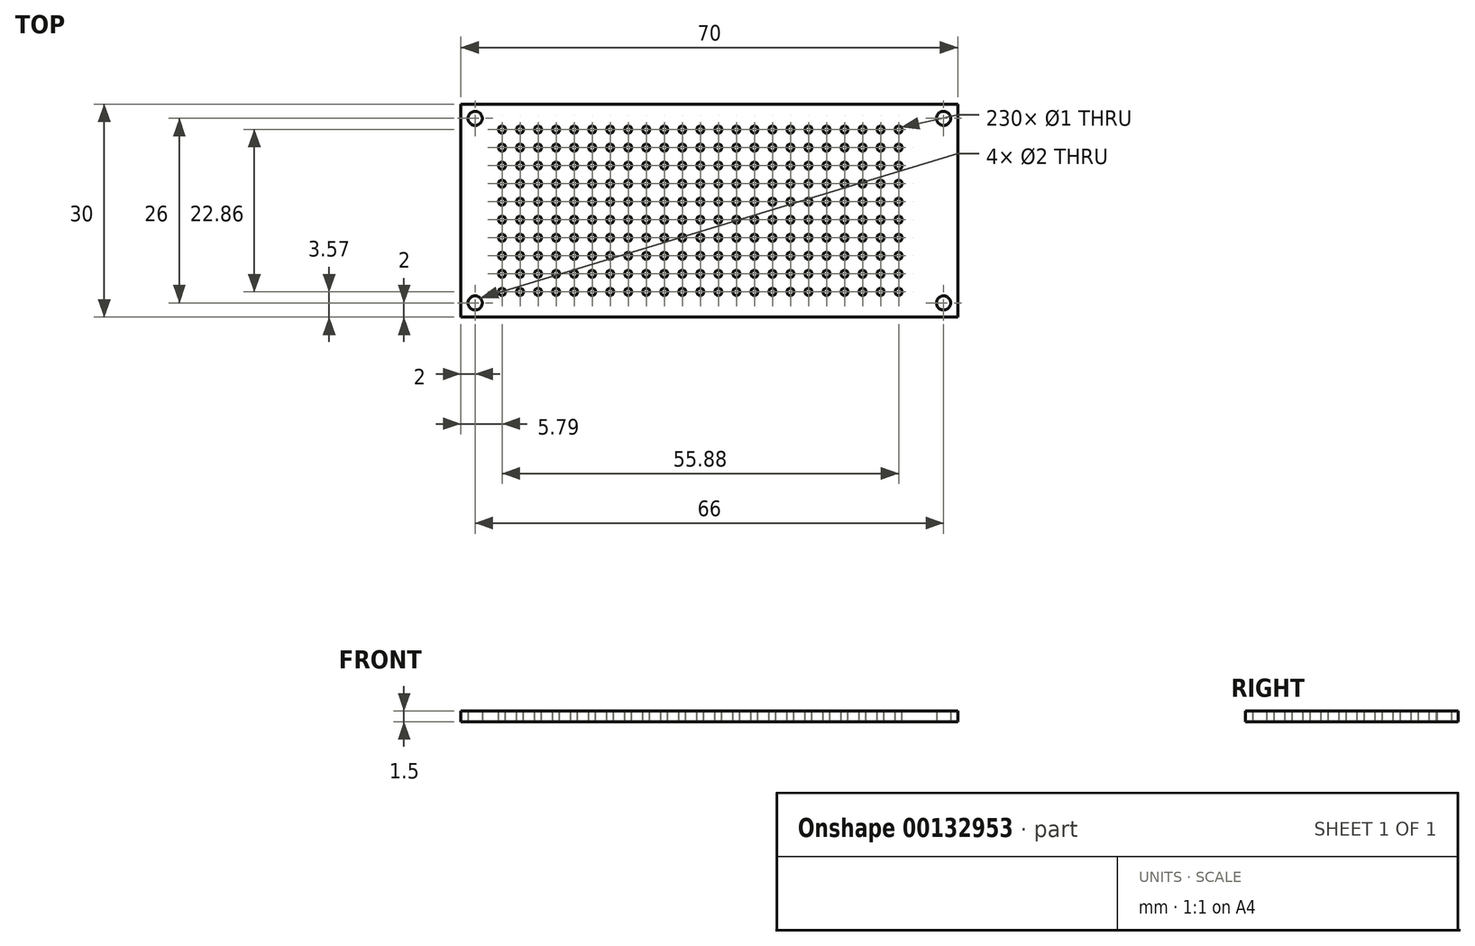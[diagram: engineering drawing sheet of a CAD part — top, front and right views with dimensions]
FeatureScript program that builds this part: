
annotation { "Feature Type Name" : "Feature", "Feature Type Description" : "" }
export const myFeature = defineFeature(function(context is Context, id is Id, definition is map)
    precondition{}
    {
        {
            var Q0;
            Q0=qCreatedBy(makeId("Top.planeOp"),FACE);
            var sketch = newSketch(context, id + "F0", { "sketchPlane" : qUnion([Q0])});
            skLineSegment(sketch, "E0.bottom", {"start": v(0, 0) * mm, "end": v(70, 0) * mm});
            skLineSegment(sketch, "E0.top", {"start": v(0, 30) * mm, "end": v(70, 30) * mm});
            skLineSegment(sketch, "E0.left", {"start": v(0, 0) * mm, "end": v(0, 30) * mm});
            skLineSegment(sketch, "E0.right", {"start": v(70, 0) * mm, "end": v(70, 30) * mm});
            skLineSegment(sketch, "E1.bottom", {"start": v(2, 28) * mm, "end": v(68, 28) * mm, "construction": true});
            skLineSegment(sketch, "E1.top", {"start": v(2, 2) * mm, "end": v(68, 2) * mm, "construction": true});
            skLineSegment(sketch, "E1.left", {"start": v(2, 28) * mm, "end": v(2, 2) * mm, "construction": true});
            skLineSegment(sketch, "E1.right", {"start": v(68, 28) * mm, "end": v(68, 2) * mm, "construction": true});
            skCircle(sketch, "E2", {"center": v(2, 28) * mm, "radius": 1 * mm});
            skCircle(sketch, "E3", {"center": v(68, 28) * mm, "radius": 1 * mm});
            skCircle(sketch, "E4", {"center": v(68, 2) * mm, "radius": 1 * mm});
            skCircle(sketch, "E5", {"center": v(2, 2) * mm, "radius": 1 * mm});
            skSolve(sketch);
        }
        {
            var Q0;
            Q0 = qSketchRegion(id + "F0", true);
            extrude(context, id + "F1", {"entities" : qUnion([Q0]), "depth" : 1.5 * mm});
        }
        {
            var Q0;
            Q0=makeQuery(id+"F1.opExtrude","CAP_FACE",FACE,{"disambiguationData":[OSD([sQuery(id+"F0.wireOp",EDGE,"E0.bottom"),sQuery(id+"F0.wireOp",EDGE,"E0.top"),sQuery(id+"F0.wireOp",EDGE,"E0.left"),sQuery(id+"F0.wireOp",EDGE,"E0.right"),sQuery(id+"F0.wireOp",EDGE,"E2"),sQuery(id+"F0.wireOp",EDGE,"E3"),sQuery(id+"F0.wireOp",EDGE,"E4"),sQuery(id+"F0.wireOp",EDGE,"E5")])],"isStart":false});
            var sketch = newSketch(context, id + "F2", { "sketchPlane" : qUnion([Q0])});
            skLineSegment(sketch, "E6", {"start": v(5.79, 30) * mm, "end": v(5.79, 26.43) * mm, "construction": true});
            skLineSegment(sketch, "E7", {"start": v(5.79, 26.43) * mm, "end": v(5.79, 23.9) * mm, "construction": true});
            skLineSegment(sketch, "E8", {"start": v(5.79, 26.43) * mm, "end": v(0, 26.43) * mm, "construction": true});
            skLineSegment(sketch, "E9", {"start": v(5.79, 26.43) * mm, "end": v(8.33, 26.43) * mm, "construction": true});
            skLineSegment(sketch, "E10.1.0.0", {"start": v(8.33, 26.43) * mm, "end": v(10.87, 26.43) * mm, "construction": true});
            skLineSegment(sketch, "E10.2.0.0", {"start": v(10.87, 26.43) * mm, "end": v(13.4, 26.43) * mm, "construction": true});
            skLineSegment(sketch, "E10.3.0.0", {"start": v(13.4, 26.43) * mm, "end": v(15.95, 26.43) * mm, "construction": true});
            skLineSegment(sketch, "E10.4.0.0", {"start": v(15.95, 26.43) * mm, "end": v(18.49, 26.43) * mm, "construction": true});
            skLineSegment(sketch, "E10.5.0.0", {"start": v(18.49, 26.43) * mm, "end": v(21.03, 26.43) * mm, "construction": true});
            skLineSegment(sketch, "E10.6.0.0", {"start": v(21.03, 26.43) * mm, "end": v(23.57, 26.43) * mm, "construction": true});
            skLineSegment(sketch, "E10.7.0.0", {"start": v(23.57, 26.43) * mm, "end": v(26.11, 26.43) * mm, "construction": true});
            skLineSegment(sketch, "E10.8.0.0", {"start": v(26.11, 26.43) * mm, "end": v(28.65, 26.43) * mm, "construction": true});
            skLineSegment(sketch, "E10.9.0.0", {"start": v(28.65, 26.43) * mm, "end": v(31.2, 26.43) * mm, "construction": true});
            skLineSegment(sketch, "E10.10.0.0", {"start": v(31.2, 26.43) * mm, "end": v(33.73, 26.43) * mm, "construction": true});
            skLineSegment(sketch, "E10.11.0.0", {"start": v(33.73, 26.43) * mm, "end": v(36.27, 26.43) * mm, "construction": true});
            skLineSegment(sketch, "E10.12.0.0", {"start": v(36.27, 26.43) * mm, "end": v(38.81, 26.43) * mm, "construction": true});
            skLineSegment(sketch, "E10.13.0.0", {"start": v(38.81, 26.43) * mm, "end": v(41.35, 26.43) * mm, "construction": true});
            skLineSegment(sketch, "E10.14.0.0", {"start": v(41.35, 26.43) * mm, "end": v(43.9, 26.43) * mm, "construction": true});
            skLineSegment(sketch, "E10.15.0.0", {"start": v(43.9, 26.43) * mm, "end": v(46.43, 26.43) * mm, "construction": true});
            skLineSegment(sketch, "E10.16.0.0", {"start": v(46.43, 26.43) * mm, "end": v(48.97, 26.43) * mm, "construction": true});
            skLineSegment(sketch, "E10.17.0.0", {"start": v(48.97, 26.43) * mm, "end": v(51.51, 26.43) * mm, "construction": true});
            skLineSegment(sketch, "E10.18.0.0", {"start": v(51.51, 26.43) * mm, "end": v(54.05, 26.43) * mm, "construction": true});
            skLineSegment(sketch, "E10.19.0.0", {"start": v(54.05, 26.43) * mm, "end": v(56.6, 26.43) * mm, "construction": true});
            skLineSegment(sketch, "E10.20.0.0", {"start": v(56.6, 26.43) * mm, "end": v(59.13, 26.43) * mm, "construction": true});
            skLineSegment(sketch, "E10.21.0.0", {"start": v(59.13, 26.43) * mm, "end": v(61.67, 26.43) * mm, "construction": true});
            skLineSegment(sketch, "E10.22.0.0", {"start": v(61.67, 26.43) * mm, "end": v(64.21, 26.43) * mm, "construction": true});
            skLineSegment(sketch, "E11", {"start": v(64.21, 26.43) * mm, "end": v(70, 26.43) * mm, "construction": true});
            skLineSegment(sketch, "E12.0.1.0", {"start": v(5.79, 23.9) * mm, "end": v(5.79, 21.35) * mm, "construction": true});
            skLineSegment(sketch, "E12.0.2.0", {"start": v(5.79, 21.35) * mm, "end": v(5.79, 18.8) * mm, "construction": true});
            skLineSegment(sketch, "E12.0.3.0", {"start": v(5.79, 18.8) * mm, "end": v(5.79, 16.27) * mm, "construction": true});
            skLineSegment(sketch, "E12.0.4.0", {"start": v(5.79, 16.27) * mm, "end": v(5.79, 13.73) * mm, "construction": true});
            skLineSegment(sketch, "E12.0.5.0", {"start": v(5.79, 13.73) * mm, "end": v(5.79, 11.19) * mm, "construction": true});
            skLineSegment(sketch, "E12.0.6.0", {"start": v(5.79, 11.19) * mm, "end": v(5.79, 8.65) * mm, "construction": true});
            skLineSegment(sketch, "E12.0.7.0", {"start": v(5.79, 8.65) * mm, "end": v(5.79, 6.1) * mm, "construction": true});
            skLineSegment(sketch, "E12.0.8.0", {"start": v(5.79, 6.1) * mm, "end": v(5.79, 3.57) * mm, "construction": true});
            skLineSegment(sketch, "E12.direction1", {"start": v(5.79, 23.9) * mm, "end": v(29.52, 23.9) * mm, "construction": true});
            skLineSegment(sketch, "E12.direction2", {"start": v(5.79, 23.9) * mm, "end": v(5.79, 21.35) * mm, "construction": true});
            skLineSegment(sketch, "E13", {"start": v(5.79, 3.57) * mm, "end": v(5.79, 0) * mm, "construction": true});
            skCircle(sketch, "E14", {"center": v(5.79, 26.43) * mm, "radius": 0.5 * mm});
            skCircle(sketch, "E15.0.1.0", {"center": v(5.79, 23.9) * mm, "radius": 0.5 * mm});
            skCircle(sketch, "E15.0.2.0", {"center": v(5.79, 21.35) * mm, "radius": 0.5 * mm});
            skCircle(sketch, "E15.0.3.0", {"center": v(5.79, 18.8) * mm, "radius": 0.5 * mm});
            skCircle(sketch, "E15.0.4.0", {"center": v(5.79, 16.27) * mm, "radius": 0.5 * mm});
            skCircle(sketch, "E15.0.5.0", {"center": v(5.79, 13.73) * mm, "radius": 0.5 * mm});
            skCircle(sketch, "E15.0.6.0", {"center": v(5.79, 11.19) * mm, "radius": 0.5 * mm});
            skCircle(sketch, "E15.0.7.0", {"center": v(5.79, 8.65) * mm, "radius": 0.5 * mm});
            skCircle(sketch, "E15.0.8.0", {"center": v(5.79, 6.1) * mm, "radius": 0.5 * mm});
            skCircle(sketch, "E15.0.9.0", {"center": v(5.79, 3.57) * mm, "radius": 0.5 * mm});
            skCircle(sketch, "E15.1.0.0", {"center": v(8.33, 26.43) * mm, "radius": 0.5 * mm});
            skCircle(sketch, "E15.1.1.0", {"center": v(8.33, 23.9) * mm, "radius": 0.5 * mm});
            skCircle(sketch, "E15.1.2.0", {"center": v(8.33, 21.35) * mm, "radius": 0.5 * mm});
            skCircle(sketch, "E15.1.3.0", {"center": v(8.33, 18.8) * mm, "radius": 0.5 * mm});
            skCircle(sketch, "E15.1.4.0", {"center": v(8.33, 16.27) * mm, "radius": 0.5 * mm});
            skCircle(sketch, "E15.1.5.0", {"center": v(8.33, 13.73) * mm, "radius": 0.5 * mm});
            skCircle(sketch, "E15.1.6.0", {"center": v(8.33, 11.19) * mm, "radius": 0.5 * mm});
            skCircle(sketch, "E15.1.7.0", {"center": v(8.33, 8.65) * mm, "radius": 0.5 * mm});
            skCircle(sketch, "E15.1.8.0", {"center": v(8.33, 6.1) * mm, "radius": 0.5 * mm});
            skCircle(sketch, "E15.1.9.0", {"center": v(8.33, 3.57) * mm, "radius": 0.5 * mm});
            skCircle(sketch, "E15.2.0.0", {"center": v(10.87, 26.43) * mm, "radius": 0.5 * mm});
            skCircle(sketch, "E15.2.1.0", {"center": v(10.87, 23.9) * mm, "radius": 0.5 * mm});
            skCircle(sketch, "E15.2.2.0", {"center": v(10.87, 21.35) * mm, "radius": 0.5 * mm});
            skCircle(sketch, "E15.2.3.0", {"center": v(10.87, 18.8) * mm, "radius": 0.5 * mm});
            skCircle(sketch, "E15.2.4.0", {"center": v(10.87, 16.27) * mm, "radius": 0.5 * mm});
            skCircle(sketch, "E15.2.5.0", {"center": v(10.87, 13.73) * mm, "radius": 0.5 * mm});
            skCircle(sketch, "E15.2.6.0", {"center": v(10.87, 11.19) * mm, "radius": 0.5 * mm});
            skCircle(sketch, "E15.2.7.0", {"center": v(10.87, 8.65) * mm, "radius": 0.5 * mm});
            skCircle(sketch, "E15.2.8.0", {"center": v(10.87, 6.1) * mm, "radius": 0.5 * mm});
            skCircle(sketch, "E15.2.9.0", {"center": v(10.87, 3.57) * mm, "radius": 0.5 * mm});
            skCircle(sketch, "E15.3.0.0", {"center": v(13.4, 26.43) * mm, "radius": 0.5 * mm});
            skCircle(sketch, "E15.3.1.0", {"center": v(13.4, 23.9) * mm, "radius": 0.5 * mm});
            skCircle(sketch, "E15.3.2.0", {"center": v(13.4, 21.35) * mm, "radius": 0.5 * mm});
            skCircle(sketch, "E15.3.3.0", {"center": v(13.4, 18.8) * mm, "radius": 0.5 * mm});
            skCircle(sketch, "E15.3.4.0", {"center": v(13.4, 16.27) * mm, "radius": 0.5 * mm});
            skCircle(sketch, "E15.3.5.0", {"center": v(13.4, 13.73) * mm, "radius": 0.5 * mm});
            skCircle(sketch, "E15.3.6.0", {"center": v(13.4, 11.19) * mm, "radius": 0.5 * mm});
            skCircle(sketch, "E15.3.7.0", {"center": v(13.4, 8.65) * mm, "radius": 0.5 * mm});
            skCircle(sketch, "E15.3.8.0", {"center": v(13.4, 6.1) * mm, "radius": 0.5 * mm});
            skCircle(sketch, "E15.3.9.0", {"center": v(13.4, 3.57) * mm, "radius": 0.5 * mm});
            skCircle(sketch, "E15.4.0.0", {"center": v(15.95, 26.43) * mm, "radius": 0.5 * mm});
            skCircle(sketch, "E15.4.1.0", {"center": v(15.95, 23.9) * mm, "radius": 0.5 * mm});
            skCircle(sketch, "E15.4.2.0", {"center": v(15.95, 21.35) * mm, "radius": 0.5 * mm});
            skCircle(sketch, "E15.4.3.0", {"center": v(15.95, 18.8) * mm, "radius": 0.5 * mm});
            skCircle(sketch, "E15.4.4.0", {"center": v(15.95, 16.27) * mm, "radius": 0.5 * mm});
            skCircle(sketch, "E15.4.5.0", {"center": v(15.95, 13.73) * mm, "radius": 0.5 * mm});
            skCircle(sketch, "E15.4.6.0", {"center": v(15.95, 11.19) * mm, "radius": 0.5 * mm});
            skCircle(sketch, "E15.4.7.0", {"center": v(15.95, 8.65) * mm, "radius": 0.5 * mm});
            skCircle(sketch, "E15.4.8.0", {"center": v(15.95, 6.1) * mm, "radius": 0.5 * mm});
            skCircle(sketch, "E15.4.9.0", {"center": v(15.95, 3.57) * mm, "radius": 0.5 * mm});
            skCircle(sketch, "E15.5.0.0", {"center": v(18.49, 26.43) * mm, "radius": 0.5 * mm});
            skCircle(sketch, "E15.5.1.0", {"center": v(18.49, 23.9) * mm, "radius": 0.5 * mm});
            skCircle(sketch, "E15.5.2.0", {"center": v(18.49, 21.35) * mm, "radius": 0.5 * mm});
            skCircle(sketch, "E15.5.3.0", {"center": v(18.49, 18.8) * mm, "radius": 0.5 * mm});
            skCircle(sketch, "E15.5.4.0", {"center": v(18.49, 16.27) * mm, "radius": 0.5 * mm});
            skCircle(sketch, "E15.5.5.0", {"center": v(18.49, 13.73) * mm, "radius": 0.5 * mm});
            skCircle(sketch, "E15.5.6.0", {"center": v(18.49, 11.19) * mm, "radius": 0.5 * mm});
            skCircle(sketch, "E15.5.7.0", {"center": v(18.49, 8.65) * mm, "radius": 0.5 * mm});
            skCircle(sketch, "E15.5.8.0", {"center": v(18.49, 6.1) * mm, "radius": 0.5 * mm});
            skCircle(sketch, "E15.5.9.0", {"center": v(18.49, 3.57) * mm, "radius": 0.5 * mm});
            skCircle(sketch, "E15.6.0.0", {"center": v(21.03, 26.43) * mm, "radius": 0.5 * mm});
            skCircle(sketch, "E15.6.1.0", {"center": v(21.03, 23.9) * mm, "radius": 0.5 * mm});
            skCircle(sketch, "E15.6.2.0", {"center": v(21.03, 21.35) * mm, "radius": 0.5 * mm});
            skCircle(sketch, "E15.6.3.0", {"center": v(21.03, 18.8) * mm, "radius": 0.5 * mm});
            skCircle(sketch, "E15.6.4.0", {"center": v(21.03, 16.27) * mm, "radius": 0.5 * mm});
            skCircle(sketch, "E15.6.5.0", {"center": v(21.03, 13.73) * mm, "radius": 0.5 * mm});
            skCircle(sketch, "E15.6.6.0", {"center": v(21.03, 11.19) * mm, "radius": 0.5 * mm});
            skCircle(sketch, "E15.6.7.0", {"center": v(21.03, 8.65) * mm, "radius": 0.5 * mm});
            skCircle(sketch, "E15.6.8.0", {"center": v(21.03, 6.1) * mm, "radius": 0.5 * mm});
            skCircle(sketch, "E15.6.9.0", {"center": v(21.03, 3.57) * mm, "radius": 0.5 * mm});
            skCircle(sketch, "E15.7.0.0", {"center": v(23.57, 26.43) * mm, "radius": 0.5 * mm});
            skCircle(sketch, "E15.7.1.0", {"center": v(23.57, 23.9) * mm, "radius": 0.5 * mm});
            skCircle(sketch, "E15.7.2.0", {"center": v(23.57, 21.35) * mm, "radius": 0.5 * mm});
            skCircle(sketch, "E15.7.3.0", {"center": v(23.57, 18.8) * mm, "radius": 0.5 * mm});
            skCircle(sketch, "E15.7.4.0", {"center": v(23.57, 16.27) * mm, "radius": 0.5 * mm});
            skCircle(sketch, "E15.7.5.0", {"center": v(23.57, 13.73) * mm, "radius": 0.5 * mm});
            skCircle(sketch, "E15.7.6.0", {"center": v(23.57, 11.19) * mm, "radius": 0.5 * mm});
            skCircle(sketch, "E15.7.7.0", {"center": v(23.57, 8.65) * mm, "radius": 0.5 * mm});
            skCircle(sketch, "E15.7.8.0", {"center": v(23.57, 6.1) * mm, "radius": 0.5 * mm});
            skCircle(sketch, "E15.7.9.0", {"center": v(23.57, 3.57) * mm, "radius": 0.5 * mm});
            skCircle(sketch, "E15.8.0.0", {"center": v(26.11, 26.43) * mm, "radius": 0.5 * mm});
            skCircle(sketch, "E15.8.1.0", {"center": v(26.11, 23.9) * mm, "radius": 0.5 * mm});
            skCircle(sketch, "E15.8.2.0", {"center": v(26.11, 21.35) * mm, "radius": 0.5 * mm});
            skCircle(sketch, "E15.8.3.0", {"center": v(26.11, 18.8) * mm, "radius": 0.5 * mm});
            skCircle(sketch, "E15.8.4.0", {"center": v(26.11, 16.27) * mm, "radius": 0.5 * mm});
            skCircle(sketch, "E15.8.5.0", {"center": v(26.11, 13.73) * mm, "radius": 0.5 * mm});
            skCircle(sketch, "E15.8.6.0", {"center": v(26.11, 11.19) * mm, "radius": 0.5 * mm});
            skCircle(sketch, "E15.8.7.0", {"center": v(26.11, 8.65) * mm, "radius": 0.5 * mm});
            skCircle(sketch, "E15.8.8.0", {"center": v(26.11, 6.1) * mm, "radius": 0.5 * mm});
            skCircle(sketch, "E15.8.9.0", {"center": v(26.11, 3.57) * mm, "radius": 0.5 * mm});
            skCircle(sketch, "E15.9.0.0", {"center": v(28.65, 26.43) * mm, "radius": 0.5 * mm});
            skCircle(sketch, "E15.9.1.0", {"center": v(28.65, 23.9) * mm, "radius": 0.5 * mm});
            skCircle(sketch, "E15.9.2.0", {"center": v(28.65, 21.35) * mm, "radius": 0.5 * mm});
            skCircle(sketch, "E15.9.3.0", {"center": v(28.65, 18.8) * mm, "radius": 0.5 * mm});
            skCircle(sketch, "E15.9.4.0", {"center": v(28.65, 16.27) * mm, "radius": 0.5 * mm});
            skCircle(sketch, "E15.9.5.0", {"center": v(28.65, 13.73) * mm, "radius": 0.5 * mm});
            skCircle(sketch, "E15.9.6.0", {"center": v(28.65, 11.19) * mm, "radius": 0.5 * mm});
            skCircle(sketch, "E15.9.7.0", {"center": v(28.65, 8.65) * mm, "radius": 0.5 * mm});
            skCircle(sketch, "E15.9.8.0", {"center": v(28.65, 6.1) * mm, "radius": 0.5 * mm});
            skCircle(sketch, "E15.9.9.0", {"center": v(28.65, 3.57) * mm, "radius": 0.5 * mm});
            skCircle(sketch, "E15.10.0.0", {"center": v(31.2, 26.43) * mm, "radius": 0.5 * mm});
            skCircle(sketch, "E15.10.1.0", {"center": v(31.2, 23.9) * mm, "radius": 0.5 * mm});
            skCircle(sketch, "E15.10.2.0", {"center": v(31.2, 21.35) * mm, "radius": 0.5 * mm});
            skCircle(sketch, "E15.10.3.0", {"center": v(31.2, 18.8) * mm, "radius": 0.5 * mm});
            skCircle(sketch, "E15.10.4.0", {"center": v(31.2, 16.27) * mm, "radius": 0.5 * mm});
            skCircle(sketch, "E15.10.5.0", {"center": v(31.2, 13.73) * mm, "radius": 0.5 * mm});
            skCircle(sketch, "E15.10.6.0", {"center": v(31.2, 11.19) * mm, "radius": 0.5 * mm});
            skCircle(sketch, "E15.10.7.0", {"center": v(31.2, 8.65) * mm, "radius": 0.5 * mm});
            skCircle(sketch, "E15.10.8.0", {"center": v(31.2, 6.1) * mm, "radius": 0.5 * mm});
            skCircle(sketch, "E15.10.9.0", {"center": v(31.2, 3.57) * mm, "radius": 0.5 * mm});
            skCircle(sketch, "E15.11.0.0", {"center": v(33.73, 26.43) * mm, "radius": 0.5 * mm});
            skCircle(sketch, "E15.11.1.0", {"center": v(33.73, 23.9) * mm, "radius": 0.5 * mm});
            skCircle(sketch, "E15.11.2.0", {"center": v(33.73, 21.35) * mm, "radius": 0.5 * mm});
            skCircle(sketch, "E15.11.3.0", {"center": v(33.73, 18.8) * mm, "radius": 0.5 * mm});
            skCircle(sketch, "E15.11.4.0", {"center": v(33.73, 16.27) * mm, "radius": 0.5 * mm});
            skCircle(sketch, "E15.11.5.0", {"center": v(33.73, 13.73) * mm, "radius": 0.5 * mm});
            skCircle(sketch, "E15.11.6.0", {"center": v(33.73, 11.19) * mm, "radius": 0.5 * mm});
            skCircle(sketch, "E15.11.7.0", {"center": v(33.73, 8.65) * mm, "radius": 0.5 * mm});
            skCircle(sketch, "E15.11.8.0", {"center": v(33.73, 6.1) * mm, "radius": 0.5 * mm});
            skCircle(sketch, "E15.11.9.0", {"center": v(33.73, 3.57) * mm, "radius": 0.5 * mm});
            skCircle(sketch, "E15.12.0.0", {"center": v(36.27, 26.43) * mm, "radius": 0.5 * mm});
            skCircle(sketch, "E15.12.1.0", {"center": v(36.27, 23.9) * mm, "radius": 0.5 * mm});
            skCircle(sketch, "E15.12.2.0", {"center": v(36.27, 21.35) * mm, "radius": 0.5 * mm});
            skCircle(sketch, "E15.12.3.0", {"center": v(36.27, 18.8) * mm, "radius": 0.5 * mm});
            skCircle(sketch, "E15.12.4.0", {"center": v(36.27, 16.27) * mm, "radius": 0.5 * mm});
            skCircle(sketch, "E15.12.5.0", {"center": v(36.27, 13.73) * mm, "radius": 0.5 * mm});
            skCircle(sketch, "E15.12.6.0", {"center": v(36.27, 11.19) * mm, "radius": 0.5 * mm});
            skCircle(sketch, "E15.12.7.0", {"center": v(36.27, 8.65) * mm, "radius": 0.5 * mm});
            skCircle(sketch, "E15.12.8.0", {"center": v(36.27, 6.1) * mm, "radius": 0.5 * mm});
            skCircle(sketch, "E15.12.9.0", {"center": v(36.27, 3.57) * mm, "radius": 0.5 * mm});
            skCircle(sketch, "E15.13.0.0", {"center": v(38.81, 26.43) * mm, "radius": 0.5 * mm});
            skCircle(sketch, "E15.13.1.0", {"center": v(38.81, 23.9) * mm, "radius": 0.5 * mm});
            skCircle(sketch, "E15.13.2.0", {"center": v(38.81, 21.35) * mm, "radius": 0.5 * mm});
            skCircle(sketch, "E15.13.3.0", {"center": v(38.81, 18.8) * mm, "radius": 0.5 * mm});
            skCircle(sketch, "E15.13.4.0", {"center": v(38.81, 16.27) * mm, "radius": 0.5 * mm});
            skCircle(sketch, "E15.13.5.0", {"center": v(38.81, 13.73) * mm, "radius": 0.5 * mm});
            skCircle(sketch, "E15.13.6.0", {"center": v(38.81, 11.19) * mm, "radius": 0.5 * mm});
            skCircle(sketch, "E15.13.7.0", {"center": v(38.81, 8.65) * mm, "radius": 0.5 * mm});
            skCircle(sketch, "E15.13.8.0", {"center": v(38.81, 6.1) * mm, "radius": 0.5 * mm});
            skCircle(sketch, "E15.13.9.0", {"center": v(38.81, 3.57) * mm, "radius": 0.5 * mm});
            skCircle(sketch, "E15.14.0.0", {"center": v(41.35, 26.43) * mm, "radius": 0.5 * mm});
            skCircle(sketch, "E15.14.1.0", {"center": v(41.35, 23.9) * mm, "radius": 0.5 * mm});
            skCircle(sketch, "E15.14.2.0", {"center": v(41.35, 21.35) * mm, "radius": 0.5 * mm});
            skCircle(sketch, "E15.14.3.0", {"center": v(41.35, 18.8) * mm, "radius": 0.5 * mm});
            skCircle(sketch, "E15.14.4.0", {"center": v(41.35, 16.27) * mm, "radius": 0.5 * mm});
            skCircle(sketch, "E15.14.5.0", {"center": v(41.35, 13.73) * mm, "radius": 0.5 * mm});
            skCircle(sketch, "E15.14.6.0", {"center": v(41.35, 11.19) * mm, "radius": 0.5 * mm});
            skCircle(sketch, "E15.14.7.0", {"center": v(41.35, 8.65) * mm, "radius": 0.5 * mm});
            skCircle(sketch, "E15.14.8.0", {"center": v(41.35, 6.1) * mm, "radius": 0.5 * mm});
            skCircle(sketch, "E15.14.9.0", {"center": v(41.35, 3.57) * mm, "radius": 0.5 * mm});
            skCircle(sketch, "E15.15.0.0", {"center": v(43.9, 26.43) * mm, "radius": 0.5 * mm});
            skCircle(sketch, "E15.15.1.0", {"center": v(43.9, 23.9) * mm, "radius": 0.5 * mm});
            skCircle(sketch, "E15.15.2.0", {"center": v(43.9, 21.35) * mm, "radius": 0.5 * mm});
            skCircle(sketch, "E15.15.3.0", {"center": v(43.9, 18.8) * mm, "radius": 0.5 * mm});
            skCircle(sketch, "E15.15.4.0", {"center": v(43.9, 16.27) * mm, "radius": 0.5 * mm});
            skCircle(sketch, "E15.15.5.0", {"center": v(43.9, 13.73) * mm, "radius": 0.5 * mm});
            skCircle(sketch, "E15.15.6.0", {"center": v(43.9, 11.19) * mm, "radius": 0.5 * mm});
            skCircle(sketch, "E15.15.7.0", {"center": v(43.9, 8.65) * mm, "radius": 0.5 * mm});
            skCircle(sketch, "E15.15.8.0", {"center": v(43.9, 6.1) * mm, "radius": 0.5 * mm});
            skCircle(sketch, "E15.15.9.0", {"center": v(43.9, 3.57) * mm, "radius": 0.5 * mm});
            skCircle(sketch, "E15.16.0.0", {"center": v(46.43, 26.43) * mm, "radius": 0.5 * mm});
            skCircle(sketch, "E15.16.1.0", {"center": v(46.43, 23.9) * mm, "radius": 0.5 * mm});
            skCircle(sketch, "E15.16.2.0", {"center": v(46.43, 21.35) * mm, "radius": 0.5 * mm});
            skCircle(sketch, "E15.16.3.0", {"center": v(46.43, 18.8) * mm, "radius": 0.5 * mm});
            skCircle(sketch, "E15.16.4.0", {"center": v(46.43, 16.27) * mm, "radius": 0.5 * mm});
            skCircle(sketch, "E15.16.5.0", {"center": v(46.43, 13.73) * mm, "radius": 0.5 * mm});
            skCircle(sketch, "E15.16.6.0", {"center": v(46.43, 11.19) * mm, "radius": 0.5 * mm});
            skCircle(sketch, "E15.16.7.0", {"center": v(46.43, 8.65) * mm, "radius": 0.5 * mm});
            skCircle(sketch, "E15.16.8.0", {"center": v(46.43, 6.1) * mm, "radius": 0.5 * mm});
            skCircle(sketch, "E15.16.9.0", {"center": v(46.43, 3.57) * mm, "radius": 0.5 * mm});
            skCircle(sketch, "E15.17.0.0", {"center": v(48.97, 26.43) * mm, "radius": 0.5 * mm});
            skCircle(sketch, "E15.17.1.0", {"center": v(48.97, 23.9) * mm, "radius": 0.5 * mm});
            skCircle(sketch, "E15.17.2.0", {"center": v(48.97, 21.35) * mm, "radius": 0.5 * mm});
            skCircle(sketch, "E15.17.3.0", {"center": v(48.97, 18.8) * mm, "radius": 0.5 * mm});
            skCircle(sketch, "E15.17.4.0", {"center": v(48.97, 16.27) * mm, "radius": 0.5 * mm});
            skCircle(sketch, "E15.17.5.0", {"center": v(48.97, 13.73) * mm, "radius": 0.5 * mm});
            skCircle(sketch, "E15.17.6.0", {"center": v(48.97, 11.19) * mm, "radius": 0.5 * mm});
            skCircle(sketch, "E15.17.7.0", {"center": v(48.97, 8.65) * mm, "radius": 0.5 * mm});
            skCircle(sketch, "E15.17.8.0", {"center": v(48.97, 6.1) * mm, "radius": 0.5 * mm});
            skCircle(sketch, "E15.17.9.0", {"center": v(48.97, 3.57) * mm, "radius": 0.5 * mm});
            skCircle(sketch, "E15.18.0.0", {"center": v(51.51, 26.43) * mm, "radius": 0.5 * mm});
            skCircle(sketch, "E15.18.1.0", {"center": v(51.51, 23.9) * mm, "radius": 0.5 * mm});
            skCircle(sketch, "E15.18.2.0", {"center": v(51.51, 21.35) * mm, "radius": 0.5 * mm});
            skCircle(sketch, "E15.18.3.0", {"center": v(51.51, 18.8) * mm, "radius": 0.5 * mm});
            skCircle(sketch, "E15.18.4.0", {"center": v(51.51, 16.27) * mm, "radius": 0.5 * mm});
            skCircle(sketch, "E15.18.5.0", {"center": v(51.51, 13.73) * mm, "radius": 0.5 * mm});
            skCircle(sketch, "E15.18.6.0", {"center": v(51.51, 11.19) * mm, "radius": 0.5 * mm});
            skCircle(sketch, "E15.18.7.0", {"center": v(51.51, 8.65) * mm, "radius": 0.5 * mm});
            skCircle(sketch, "E15.18.8.0", {"center": v(51.51, 6.1) * mm, "radius": 0.5 * mm});
            skCircle(sketch, "E15.18.9.0", {"center": v(51.51, 3.57) * mm, "radius": 0.5 * mm});
            skCircle(sketch, "E15.19.0.0", {"center": v(54.05, 26.43) * mm, "radius": 0.5 * mm});
            skCircle(sketch, "E15.19.1.0", {"center": v(54.05, 23.9) * mm, "radius": 0.5 * mm});
            skCircle(sketch, "E15.19.2.0", {"center": v(54.05, 21.35) * mm, "radius": 0.5 * mm});
            skCircle(sketch, "E15.19.3.0", {"center": v(54.05, 18.8) * mm, "radius": 0.5 * mm});
            skCircle(sketch, "E15.19.4.0", {"center": v(54.05, 16.27) * mm, "radius": 0.5 * mm});
            skCircle(sketch, "E15.19.5.0", {"center": v(54.05, 13.73) * mm, "radius": 0.5 * mm});
            skCircle(sketch, "E15.19.6.0", {"center": v(54.05, 11.19) * mm, "radius": 0.5 * mm});
            skCircle(sketch, "E15.19.7.0", {"center": v(54.05, 8.65) * mm, "radius": 0.5 * mm});
            skCircle(sketch, "E15.19.8.0", {"center": v(54.05, 6.1) * mm, "radius": 0.5 * mm});
            skCircle(sketch, "E15.19.9.0", {"center": v(54.05, 3.57) * mm, "radius": 0.5 * mm});
            skCircle(sketch, "E15.20.0.0", {"center": v(56.6, 26.43) * mm, "radius": 0.5 * mm});
            skCircle(sketch, "E15.20.1.0", {"center": v(56.6, 23.9) * mm, "radius": 0.5 * mm});
            skCircle(sketch, "E15.20.2.0", {"center": v(56.6, 21.35) * mm, "radius": 0.5 * mm});
            skCircle(sketch, "E15.20.3.0", {"center": v(56.6, 18.8) * mm, "radius": 0.5 * mm});
            skCircle(sketch, "E15.20.4.0", {"center": v(56.6, 16.27) * mm, "radius": 0.5 * mm});
            skCircle(sketch, "E15.20.5.0", {"center": v(56.6, 13.73) * mm, "radius": 0.5 * mm});
            skCircle(sketch, "E15.20.6.0", {"center": v(56.6, 11.19) * mm, "radius": 0.5 * mm});
            skCircle(sketch, "E15.20.7.0", {"center": v(56.6, 8.65) * mm, "radius": 0.5 * mm});
            skCircle(sketch, "E15.20.8.0", {"center": v(56.6, 6.1) * mm, "radius": 0.5 * mm});
            skCircle(sketch, "E15.20.9.0", {"center": v(56.6, 3.57) * mm, "radius": 0.5 * mm});
            skCircle(sketch, "E15.21.0.0", {"center": v(59.13, 26.43) * mm, "radius": 0.5 * mm});
            skCircle(sketch, "E15.21.1.0", {"center": v(59.13, 23.9) * mm, "radius": 0.5 * mm});
            skCircle(sketch, "E15.21.2.0", {"center": v(59.13, 21.35) * mm, "radius": 0.5 * mm});
            skCircle(sketch, "E15.21.3.0", {"center": v(59.13, 18.8) * mm, "radius": 0.5 * mm});
            skCircle(sketch, "E15.21.4.0", {"center": v(59.13, 16.27) * mm, "radius": 0.5 * mm});
            skCircle(sketch, "E15.21.5.0", {"center": v(59.13, 13.73) * mm, "radius": 0.5 * mm});
            skCircle(sketch, "E15.21.6.0", {"center": v(59.13, 11.19) * mm, "radius": 0.5 * mm});
            skCircle(sketch, "E15.21.7.0", {"center": v(59.13, 8.65) * mm, "radius": 0.5 * mm});
            skCircle(sketch, "E15.21.8.0", {"center": v(59.13, 6.1) * mm, "radius": 0.5 * mm});
            skCircle(sketch, "E15.21.9.0", {"center": v(59.13, 3.57) * mm, "radius": 0.5 * mm});
            skCircle(sketch, "E15.22.0.0", {"center": v(61.67, 26.43) * mm, "radius": 0.5 * mm});
            skCircle(sketch, "E15.22.1.0", {"center": v(61.67, 23.9) * mm, "radius": 0.5 * mm});
            skCircle(sketch, "E15.22.2.0", {"center": v(61.67, 21.35) * mm, "radius": 0.5 * mm});
            skCircle(sketch, "E15.22.3.0", {"center": v(61.67, 18.8) * mm, "radius": 0.5 * mm});
            skCircle(sketch, "E15.22.4.0", {"center": v(61.67, 16.27) * mm, "radius": 0.5 * mm});
            skCircle(sketch, "E15.22.5.0", {"center": v(61.67, 13.73) * mm, "radius": 0.5 * mm});
            skCircle(sketch, "E15.22.6.0", {"center": v(61.67, 11.19) * mm, "radius": 0.5 * mm});
            skCircle(sketch, "E15.22.7.0", {"center": v(61.67, 8.65) * mm, "radius": 0.5 * mm});
            skCircle(sketch, "E15.22.8.0", {"center": v(61.67, 6.1) * mm, "radius": 0.5 * mm});
            skCircle(sketch, "E15.22.9.0", {"center": v(61.67, 3.57) * mm, "radius": 0.5 * mm});
            skSolve(sketch);
        }
        {
            var Q0;
            Q0 = qSketchRegion(id + "F2", true);
            extrude(context, id + "F3", {"entities" : qUnion([Q0]), "operationType" : NewBodyOperationType.REMOVE, "endBound" : BoundingType.THROUGH_ALL, "oppositeDirection" : true, "depth" : 25 * mm});
        }
    });
